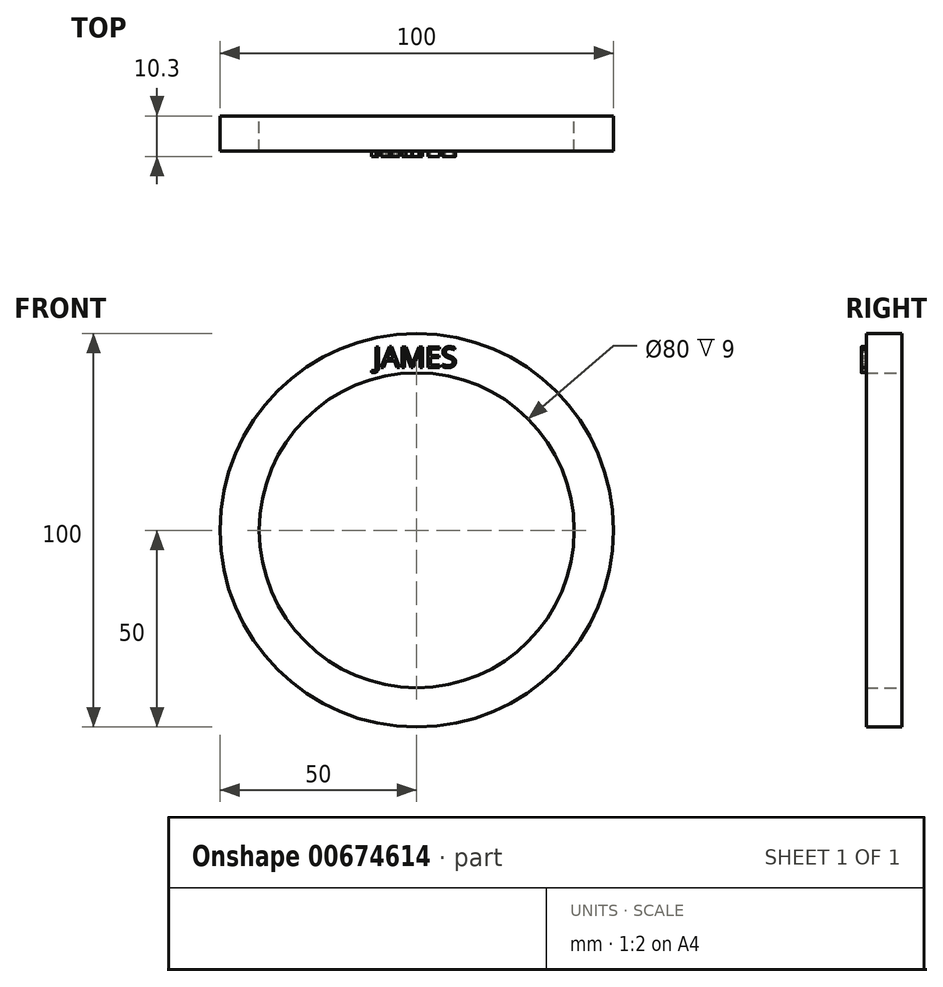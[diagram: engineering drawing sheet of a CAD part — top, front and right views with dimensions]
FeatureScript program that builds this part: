
annotation { "Feature Type Name" : "Feature", "Feature Type Description" : "" }
export const myFeature = defineFeature(function(context is Context, id is Id, definition is map)
    precondition{}
    {
        {
            var Q0;
            Q0=qCreatedBy(makeId("Front.planeOp"),FACE);
            var sketch = newSketch(context, id + "F0", { "sketchPlane" : qUnion([Q0])});
            skCircle(sketch, "E0", {"center": v(0, 0) * mm, "radius": 50 * mm});
            skCircle(sketch, "E1", {"center": v(0, 0) * mm, "radius": 40 * mm});
            skSolve(sketch);
        }
        {
            var Q0;
            Q0=makeQuery(id+"F0.imprint","IMPRINT",FACE,{"disambiguationData":[TD([[makeQuery(id+"F0.imprint","IMPRINT",EDGE,{"derivedFrom":sQuery(id+"F0.wireOp",EDGE,"E0")}),1.0]])]});
            extrude(context, id + "F1", {"entities" : qUnion([Q0]), "depth" : 9 * mm, "offsetDistance" : 25 * mm});
        }
        {
            var Q0;
            Q0=makeQuery(id+"F1.opExtrude","CAP_FACE",FACE,{"disambiguationData":[OSD([sQuery(id+"F0.wireOp",EDGE,"E0"),sQuery(id+"F0.wireOp",EDGE,"E1")])],"isStart":false});
            var sketch = newSketch(context, id + "F2", { "sketchPlane" : qUnion([Q0])});
            skText(sketch, "E2", { "text": "JAMES", "fontName": "OpenSans-Regular.ttf"});
            const initialGuessF2  = {"E2": [-0.01096, 0.04141, 1, 0, 0.00524]};
            skSetInitialGuess(sketch, initialGuessF2);
            skSolve(sketch);
        }
        {
            var Q0;
            Q0 = qSketchRegion(id + "F2", true);
            extrude(context, id + "F3", {"entities" : qUnion([Q0]), "operationType" : NewBodyOperationType.ADD, "depth" : 1.3 * mm, "offsetDistance" : 25 * mm});
        }
    });
